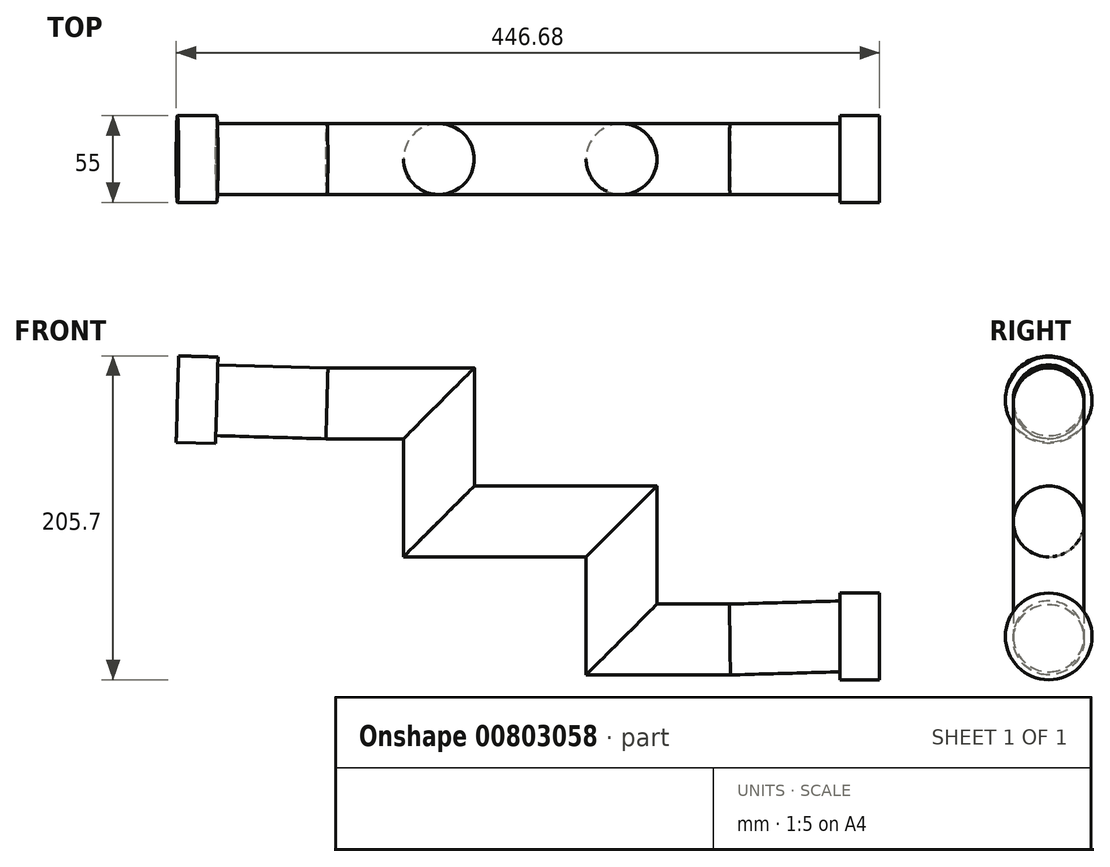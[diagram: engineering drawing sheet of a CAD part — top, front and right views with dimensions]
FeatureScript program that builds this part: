
annotation { "Feature Type Name" : "Feature", "Feature Type Description" : "" }
export const myFeature = defineFeature(function(context is Context, id is Id, definition is map)
    precondition{}
    {
        {
            var Q0;
            Q0=qCreatedBy(makeId("Front.planeOp"),FACE);
            var sketch = newSketch(context, id + "F0", { "sketchPlane" : qUnion([Q0])});
            skLineSegment(sketch, "E0", {"start": v(-58, 75) * mm, "end": v(0, 75) * mm});
            skLineSegment(sketch, "E1", {"start": v(0, 75) * mm, "end": v(0, 0) * mm});
            skLineSegment(sketch, "E2", {"start": v(0, 0) * mm, "end": v(70, 0) * mm});
            skLineSegment(sketch, "E3", {"start": v(-58, 75) * mm, "end": v(-116, 75) * mm});
            skLineSegment(sketch, "E4", {"start": v(-116, 75) * mm, "end": v(-116, 150) * mm});
            skLineSegment(sketch, "E5", {"start": v(-116, 150) * mm, "end": v(-186, 150) * mm});
            skLineSegment(sketch, "E6", {"start": v(70, 0) * mm, "end": v(139.97, 1.98) * mm});
            skSolve(sketch);
        }
        {
            var Q0;
            Q0=qCreatedBy(makeId("Right.planeOp"),FACE);
            cPlane(context, id + "F1", {"entities" : qUnion([Q0]), "cplaneType" : CPlaneType.OFFSET, "offset" : 100 * mm, "width" : 150 * mm, "height" : 150 * mm});
        }
        {
            var Q0;
            Q0=qCreatedBy(id+"F1.planeOp",FACE);
            var sketch = newSketch(context, id + "F2", { "sketchPlane" : qUnion([Q0])});
            skCircle(sketch, "E7", {"center": v(0, 1.98) * mm, "radius": 22.5 * mm});
            skSolve(sketch);
        }
        {
            var Q0;
            Q0=makeQuery(id+"F2.imprint","IMPRINT",FACE,{"disambiguationData":[TD([[makeQuery(id+"F2.imprint","IMPRINT",EDGE,{"derivedFrom":sQuery(id+"F2.wireOp",EDGE,"E7")}),1.0]])]});
            var Q1;
            Q1=sQuery(id+"F0.wireOp",EDGE,"E6");
            var Q2;
            Q2=sQuery(id+"F0.wireOp",EDGE,"E2");
            var Q3;
            Q3=sQuery(id+"F0.wireOp",EDGE,"E1");
            var Q4;
            Q4=sQuery(id+"F0.wireOp",EDGE,"E0");
            var Q5;
            Q5=sQuery(id+"F0.wireOp",EDGE,"E3");
            var Q6;
            Q6=sQuery(id+"F0.wireOp",EDGE,"E4");
            var Q7;
            Q7=sQuery(id+"F0.wireOp",EDGE,"E5");
            var Q8;
            Q8=sQuery(id+"F0.wireOp",EDGE,"P47BA6Ys-ilz4-Q5kC-EIlr-I4YoM06u4E8Z");
            sweep(context, id + "F3", {"profiles" : qUnion([Q0]), "path" : qUnion([Q1, Q2, Q3, Q4, Q5, Q6, Q7, Q8])});
        }
        {
            var Q0;
            Q0=makeQuery(id+"F3.opSweep","CAP_FACE",FACE,{"disambiguationData":[OSD([sQuery(id+"F0.wireOp",VERTEX,"P47BA6Ys-ilz4-Q5kC-EIlr-I4YoM06u4E8Z.end"),sQuery(id+"F2.wireOp",EDGE,"E7")])],"isStart":false});
            var sketch = newSketch(context, id + "F4", { "sketchPlane" : qUnion([Q0])});
            skCircle(sketch, "E8", {"center": v(0, 3.1) * mm, "radius": 27.5 * mm});
            skSolve(sketch);
        }
        {
            var Q0;
            Q0=makeQuery(id+"F4.imprint","IMPRINT",FACE,{"disambiguationData":[TD([[makeQuery(id+"F4.imprint","IMPRINT",EDGE,{"derivedFrom":sQuery(id+"F4.wireOp",EDGE,"E8")}),1.0]])]});
            var Q1;
            Q1=makeQuery(id+"F4.imprint","IMPRINT",FACE,{"disambiguationData":[TD([[makeQuery(id+"F4.imprint","IMPRINT",EDGE,{"derivedFrom":makeQuery(id+"F3.opSweep","CAP_EDGE",EDGE,{"disambiguationData":[OSD([sQuery(id+"F0.wireOp",VERTEX,"P47BA6Ys-ilz4-Q5kC-EIlr-I4YoM06u4E8Z.end"),sQuery(id+"F2.wireOp",EDGE,"E7")])],"isStart":false})}),1.0]])]});
            extrude(context, id + "F5", {"entities" : qUnion([Q0, Q1]), "operationType" : NewBodyOperationType.ADD, "depth" : 25 * mm, "offsetDistance" : 25 * mm});
        }
        {
            var Q0;
            Q0=makeQuery(id+"F3.opSweep","CAP_FACE",FACE,{"disambiguationData":[OSD([sQuery(id+"F0.wireOp",VERTEX,"E6.end"),sQuery(id+"F2.wireOp",EDGE,"E7")])],"isStart":true});
            var sketch = newSketch(context, id + "F6", { "sketchPlane" : qUnion([Q0])});
            skCircle(sketch, "E9", {"center": v(0, 145.82) * mm, "radius": 27.5 * mm});
            skSolve(sketch);
        }
        {
            var Q0;
            Q0=makeQuery(id+"F6.imprint","IMPRINT",FACE,{"disambiguationData":[TD([[makeQuery(id+"F6.imprint","IMPRINT",EDGE,{"derivedFrom":makeQuery(id+"F3.opSweep","CAP_EDGE",EDGE,{"disambiguationData":[OSD([sQuery(id+"F0.wireOp",VERTEX,"E5.end"),sQuery(id+"F2.wireOp",EDGE,"E7")])],"isStart":true})}),-1.0]])]});
            extrude(context, id + "F7", {"entities" : qUnion([Q0]), "operationType" : NewBodyOperationType.ADD, "depth" : 70 * mm, "offsetDistance" : 25 * mm});
        }
        {
            var Q0;
            Q0=makeQuery(id+"F7.opExtrude","CAP_FACE",FACE,{"disambiguationData":[OSD([sQuery(id+"F0.wireOp",VERTEX,"E5.end"),sQuery(id+"F2.wireOp",EDGE,"E7")])],"isStart":false});
            var sketch = newSketch(context, id + "F8", { "sketchPlane" : qUnion([Q0])});
            skCircle(sketch, "E10", {"center": v(0, 145.82) * mm, "radius": 27.5 * mm});
            skSolve(sketch);
        }
        {
            var Q0;
            Q0 = qSketchRegion(id + "F8", true);
            extrude(context, id + "F9", {"entities" : qUnion([Q0]), "operationType" : NewBodyOperationType.ADD, "depth" : 25 * mm, "offsetDistance" : 25 * mm});
        }
    });
